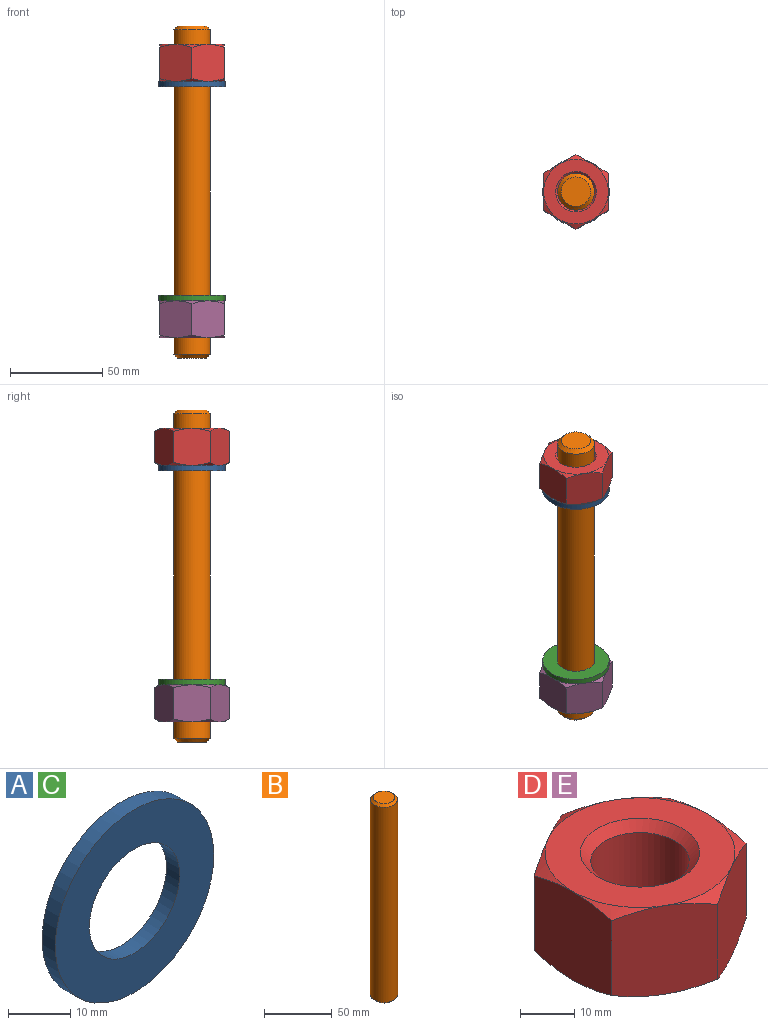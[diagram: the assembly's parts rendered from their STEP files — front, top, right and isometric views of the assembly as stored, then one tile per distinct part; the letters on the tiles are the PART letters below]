
ASSEMBLY  parts=5 mates=8
PART A: 4 faces, bbox 36x3x36 mm
  f0: cylinder r=10.25mm len=20.5mm, axis (0,1,0), area 193.2mm2, adj f2,f3
  f1: cylinder r=18mm len=36mm, axis (0,1,0), area 339.3mm2, adj f2,f3
  f2: plane 36x36mm, normal (0,-1,0), area 687.8mm2, adj f0,f1
  f3: plane 36x36mm, normal (0,1,0), area 687.8mm2, adj f0,f1
PART B: 5 faces, bbox 20x20x180 mm
  f0: cylinder r=10mm len=176mm, axis (0,0,-1), area 11058.4mm2, adj f3,f4
  f1: plane 16x16mm, normal (0,0,1), area 201.1mm2, adj f4
  f2: plane 16x16mm, normal (0,0,-1), area 201.1mm2, adj f3
  f3: cone r=10mm half-angle=45deg, axis (0,0,1), area 159.9mm2, adj f0,f2
  f4: cone r=8mm half-angle=45deg, axis (0,0,-1), area 159.9mm2, adj f0,f1
PART C: same geometry as A
PART D: 23 faces, bbox 40.4x40.4x20 mm
  f0: plane 35x35mm, normal (0,0,1), area 583.7mm2, adj f5,f6,f8,f10,f12,f14,f22
  f1: plane 35x35mm, normal (0,0,-1), area 583.7mm2, adj f3,f4,f7,f9,f11,f13,f21
  f2: cylinder r=9.07mm len=18.15mm, axis (0,0,-1), area 923.7mm2, adj f21,f22
  f3: cone r=30.53mm half-angle=60deg, axis (0,0,1), area 19mm2, adj f1,f15,f20
  f4: cone r=30.53mm half-angle=60deg, axis (0,0,1), area 19mm2, adj f1,f15,f16
  f5: cone r=30.53mm half-angle=60deg, axis (0,0,-1), area 19mm2, adj f0,f15,f20
  f6: cone r=30.53mm half-angle=60deg, axis (0,0,-1), area 19mm2, adj f0,f15,f16
  f7: cone r=30.53mm half-angle=60deg, axis (0,0,1), area 19mm2, adj f1,f16,f17
  f8: cone r=30.53mm half-angle=60deg, axis (0,0,-1), area 19mm2, adj f0,f16,f17
  f9: cone r=30.53mm half-angle=60deg, axis (0,0,1), area 19mm2, adj f1,f17,f18
  f10: cone r=30.53mm half-angle=60deg, axis (0,0,-1), area 19mm2, adj f0,f17,f18
  f11: cone r=30.53mm half-angle=60deg, axis (0,0,1), area 19mm2, adj f1,f18,f19
  f12: cone r=30.53mm half-angle=60deg, axis (0,0,-1), area 19mm2, adj f0,f18,f19
  f13: cone r=30.53mm half-angle=60deg, axis (0,0,1), area 19mm2, adj f1,f19,f20
  f14: cone r=30.53mm half-angle=60deg, axis (0,0,-1), area 19mm2, adj f0,f19,f20
  f15: plane 20.01x17.5mm, normal (-0.5,0.87,0), area 382.5mm2, adj f3,f4,f5,f6,f16,f20
  f16: plane 20.01x17.5mm, normal (0.5,0.87,0), area 382.5mm2, adj f4,f6,f7,f8,f15,f17
  f17: plane 20.22x20.02mm, normal (1,0,0), area 382.5mm2, adj f7,f8,f9,f10,f16,f18
  f18: plane 20.01x17.5mm, normal (0.5,-0.87,0), area 382.5mm2, adj f9,f10,f11,f12,f17,f19
  f19: plane 20.01x17.5mm, normal (-0.5,-0.87,0), area 382.5mm2, adj f11,f12,f13,f14,f18,f20
  f20: plane 20.22x20.02mm, normal (-1,0,0), area 382.5mm2, adj f3,f5,f13,f14,f15,f19
  f21: cone r=10.97mm half-angle=45deg, axis (0,0,-1), area 169.3mm2, adj f1,f2
  f22: cone r=9.07mm half-angle=45deg, axis (0,0,1), area 169.3mm2, adj f0,f2
PART E: same geometry as D
PLACE A rot(axis=(-1,0,0),90deg) t=(27.02,-9.79,103.91)mm
PLACE B t=(27.02,-9.79,-44.59)mm
PLACE C rot(axis=(-0.58,0.58,-0.58),120deg) t=(27.02,-9.79,-12.09)mm
PLACE D t=(27.02,-9.79,105.41)mm
PLACE E t=(27.02,-9.79,-33.59)mm
MATE cylindrical C.f0 <-> B.f0  axis (0,0,-1) through (27.02,-9.79,-12.09)mm
MATE planar A.f1 <-> C.f1  axis (0,0,-1) through (27.02,-9.79,102.41)mm
MATE planar D.f0 <-> B.f0  axis (0,0,1) through (18.27,-24.94,125.41)mm
MATE planar D.f1 <-> A.f1  axis (0,0,-1) through (18.27,5.37,105.41)mm
MATE cylindrical D.f2 <-> B.f0  axis (0,0,-1) through (27.02,-9.79,107.31)mm
MATE planar C.f1 <-> E.f3  axis (0,0,-1) through (27.02,-9.79,-13.59)mm
MATE cylindrical B.f0 <-> E.f2  axis (0,0,-1) through (27.02,-9.79,-42.59)mm
MATE cylindrical A.f0 <-> B.f0  axis (0,0,-1) through (27.02,-9.79,103.91)mm
